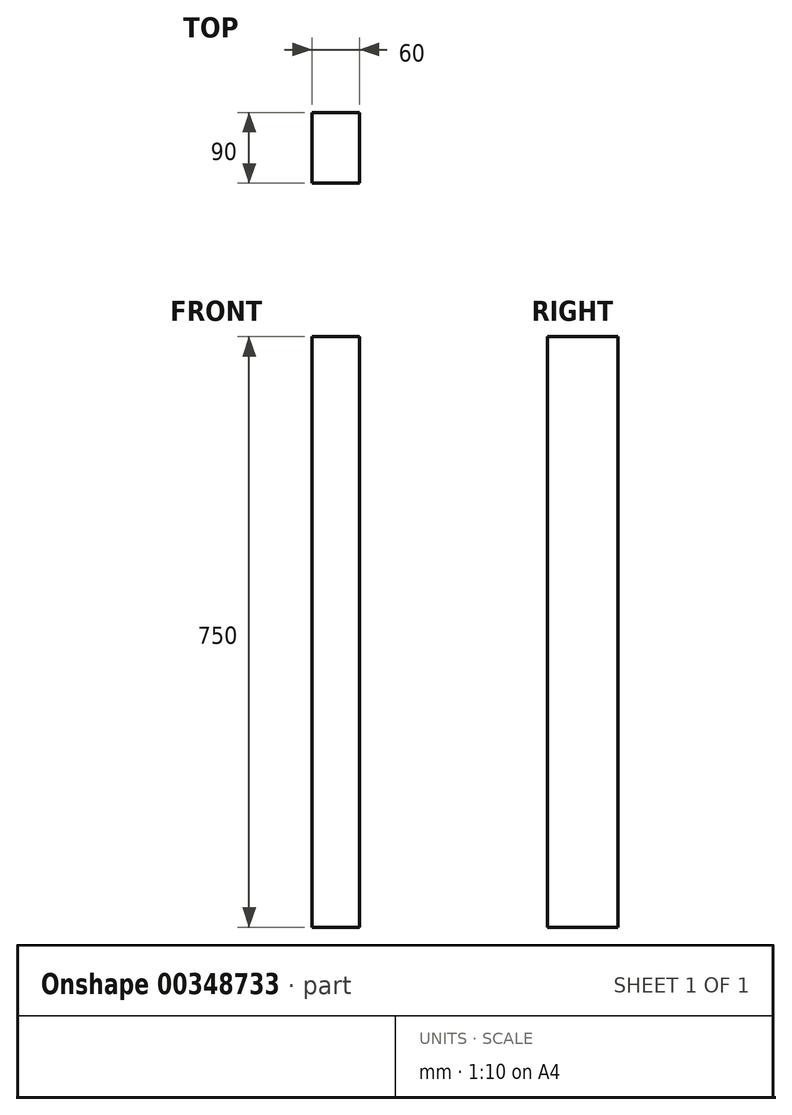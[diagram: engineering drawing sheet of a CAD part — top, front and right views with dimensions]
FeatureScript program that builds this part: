
annotation { "Feature Type Name" : "Feature", "Feature Type Description" : "" }
export const myFeature = defineFeature(function(context is Context, id is Id, definition is map)
    precondition{}
    {
        {
            var Q0;
            Q0=qCreatedBy(makeId("Right.planeOp"),FACE);
            var sketch = newSketch(context, id + "F0", { "sketchPlane" : qUnion([Q0])});
            skLineSegment(sketch, "E0.bottom", {"start": v(0, 0) * mm, "end": v(90, 0) * mm});
            skLineSegment(sketch, "E0.top", {"start": v(0, -750) * mm, "end": v(90, -750) * mm});
            skLineSegment(sketch, "E0.left", {"start": v(0, 0) * mm, "end": v(0, -750) * mm});
            skLineSegment(sketch, "E0.right", {"start": v(90, 0) * mm, "end": v(90, -750) * mm});
            skSolve(sketch);
        }
        {
            var Q0;
            Q0=makeQuery(id+"F0.imprint","IMPRINT",FACE,{"disambiguationData":[TD([[makeQuery(id+"F0.imprint","IMPRINT",EDGE,{"derivedFrom":sQuery(id+"F0.wireOp",EDGE,"E0.bottom")}),-1.0]])]});
            extrude(context, id + "F1", {"entities" : qUnion([Q0]), "depth" : 60 * mm});
        }
    });
